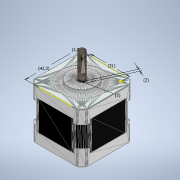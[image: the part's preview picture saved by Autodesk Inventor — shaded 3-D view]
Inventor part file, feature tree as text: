
AUTODESK INVENTOR PART (.ipt)
format: ipt  version: 2022.2 (Build 262287000, 287)  size: 1,189,888 bytes
history: native  units: mm
features: other x2, sketch x1
ambient origin geometry x8: Origin, YZ Plane, XZ Plane, XY Plane, X Axis, Y Axis, Z Axis, Center Point
feature tree (3):
  other  "17HM15-0904S"
  sketch  "Sketch1"
  other  "MeshFeature1"
